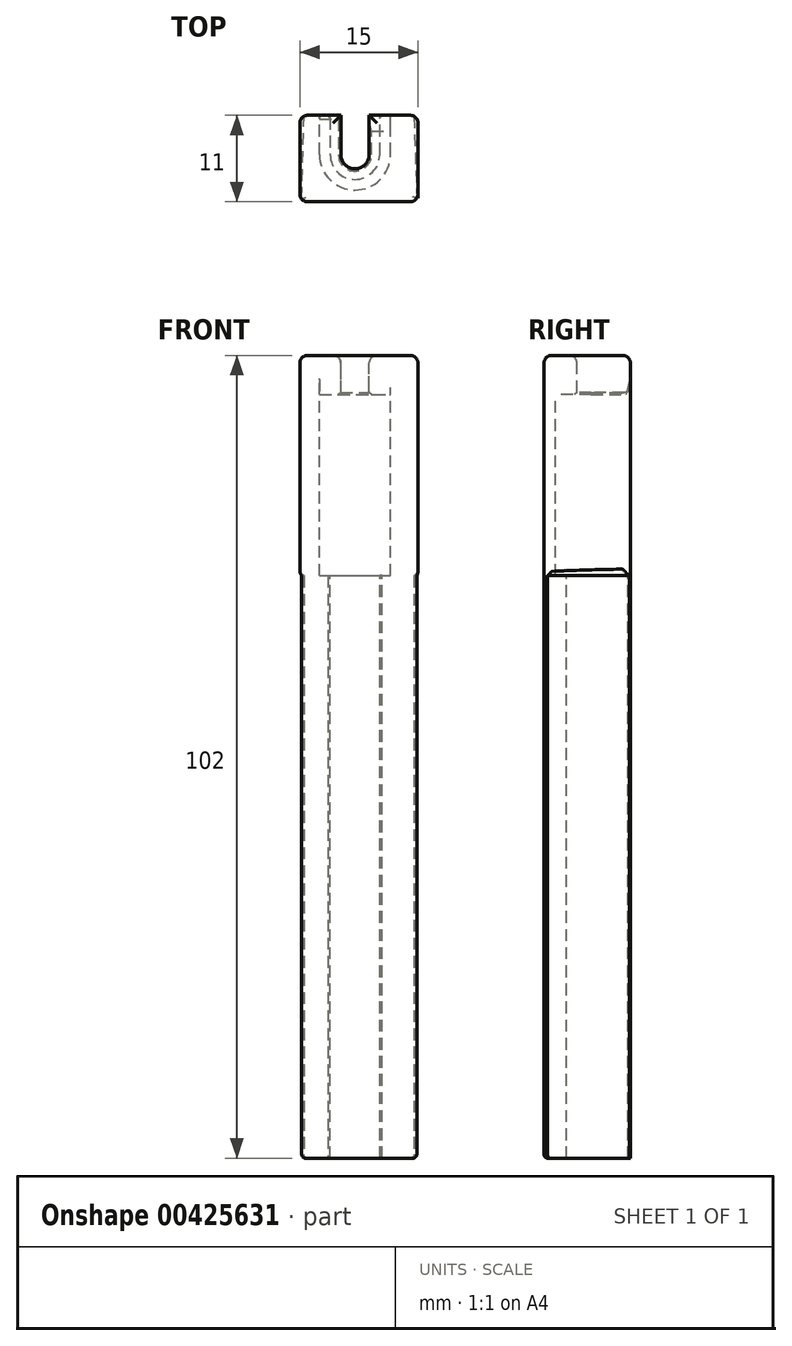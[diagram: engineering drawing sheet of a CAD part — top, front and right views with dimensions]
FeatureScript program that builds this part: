
annotation { "Feature Type Name" : "Feature", "Feature Type Description" : "" }
export const myFeature = defineFeature(function(context is Context, id is Id, definition is map)
    precondition{}
    {
        {
            var Q0;
            Q0=qCreatedBy(makeId("Top.planeOp"),FACE);
            var sketch = newSketch(context, id + "F0", { "sketchPlane" : qUnion([Q0])});
            skLineSegment(sketch, "E0", {"start": v(0, 0) * mm, "end": v(0, 20) * mm});
            skLineSegment(sketch, "E1", {"start": v(0, 20) * mm, "end": v(15, 20) * mm});
            skLineSegment(sketch, "E2", {"start": v(15, 20) * mm, "end": v(15, 0) * mm});
            skLineSegment(sketch, "E3", {"start": v(15, 0) * mm, "end": v(0, 0) * mm});
            skLineSegment(sketch, "E4", {"start": v(0, 11) * mm, "end": v(15, 11) * mm});
            skLineSegment(sketch, "E5", {"start": v(15, 16) * mm, "end": v(0, 16) * mm});
            skSolve(sketch);
        }
        {
            var Q0;
            {var subQ0=sQuery(id+"F0.wireOp",EDGE,"E3");Q0=makeQuery(id+"F0.imprint","IMPRINT",FACE,{"disambiguationData":[TD([[makeQuery(id+"F0.imprint","IMPRINT",EDGE,{"derivedFrom":subQ0}),-1.0]])]});}
            extrude(context, id + "F1", {"entities" : qUnion([Q0]), "depth" : 74 * mm});
        }
        {
            var Q0;
            Q0=makeQuery(id+"F1.opExtrude","CAP_FACE",FACE,{"disambiguationData":[OSD([sQuery(id+"F0.wireOp",EDGE,"E0"),sQuery(id+"F0.wireOp",EDGE,"E1"),sQuery(id+"F0.wireOp",EDGE,"E2"),sQuery(id+"F0.wireOp",EDGE,"E3")])],"isStart":false});
            var sketch = newSketch(context, id + "F2", { "sketchPlane" : qUnion([Q0])});
            skLineSegment(sketch, "E6", {"start": v(7, 11) * mm, "end": v(7, 0) * mm, "construction": true});
            skCircle(sketch, "E7", {"center": v(7, 6) * mm, "radius": 3.15 * mm});
            skLineSegment(sketch, "E8", {"start": v(3.85, 6) * mm, "end": v(3.85, 11) * mm});
            skLineSegment(sketch, "E9", {"start": v(10.15, 6) * mm, "end": v(10.15, 11) * mm});
            skLineSegment(sketch, "E10", {"start": v(10.15, 6) * mm, "end": v(3.85, 6) * mm, "construction": true});
            skSolve(sketch);
        }
        {
            var Q0;
            {var subQ0=sQuery(id+"F2.wireOp",EDGE,"E7");var subQ1=makeQuery(id+"F2.imprint","INTERSECT",VERTEX,{"derivedFrom":[subQ0,sQuery(id+"F2.wireOp",EDGE,"E8")]});Q0=makeQuery(id+"F2.imprint","IMPRINT",FACE,{"disambiguationData":[TD([[makeQuery(id+"F2.imprint","IMPRINT",EDGE,{"disambiguationData":[TD([[subQ1,1.0]])],"derivedFrom":subQ0}),1.0]])]});}
            var Q1;
            {var subQ0=sQuery(id+"F2.wireOp",EDGE,"E8");Q1=makeQuery(id+"F2.imprint","IMPRINT",FACE,{"disambiguationData":[TD([[makeQuery(id+"F2.imprint","IMPRINT",EDGE,{"derivedFrom":subQ0}),-1.0]])]});}
            var Q2;
            {var subQ0=sQuery(id+"F2.wireOp",EDGE,"mLhPDnLy-3AhW-8mAD-WIRb-GXeNga6SbxnZ");var subQ1=sQuery(id+"F2.wireOp",EDGE,"E8");var subQ2=makeQuery(id+"F2.imprint","INTERSECT",VERTEX,{"disambiguationData":[OD(0.0)],"derivedFrom":[subQ1,subQ0]});Q2=makeQuery(id+"F2.imprint","IMPRINT",FACE,{"disambiguationData":[TD([[makeQuery(id+"F2.imprint","IMPRINT",EDGE,{"disambiguationData":[TD([[subQ2,-1.0]])],"derivedFrom":subQ1}),-1.0]])]});}
            var Q3;
            {var subQ0=sQuery(id+"F2.wireOp",EDGE,"llRZHJFs-Bipk-uS7y-r4k3-r3Pt3Prqutk8");var subQ1=sQuery(id+"F2.wireOp",EDGE,"E9");var subQ2=makeQuery(id+"F2.imprint","INTERSECT",VERTEX,{"disambiguationData":[OD(0.0)],"derivedFrom":[subQ1,subQ0]});Q3=makeQuery(id+"F2.imprint","IMPRINT",FACE,{"disambiguationData":[TD([[makeQuery(id+"F2.imprint","IMPRINT",EDGE,{"disambiguationData":[TD([[subQ2,-1.0]])],"derivedFrom":subQ1}),1.0]])]});}
            extrude(context, id + "F3", {"entities" : qUnion([Q0, Q1, Q2, Q3]), "operationType" : NewBodyOperationType.REMOVE, "endBound" : BoundingType.UP_TO_NEXT, "oppositeDirection" : true, "depth" : 25 * mm});
        }
        {
            var Q0;
            Q0=makeQuery(id+"F1.opExtrude","SWEPT_EDGE",EDGE,{"disambiguationData":[OSD([sQuery(id+"F0.wireOp",EDGE,"E0"),sQuery(id+"F0.wireOp",EDGE,"E4")])]});
            chamfer(context, id + "F4", {"entities" : qUnion([Q0]), "chamferType" : ChamferType.TWO_OFFSETS, "width1" : 20 * mm, "oppositeDirection" : false, "width2" : .5 * mm, "tangentPropagation" : true});
        }
        {
            var Q0;
            Q0=makeQuery(id+"F1.opExtrude","SWEPT_EDGE",EDGE,{"disambiguationData":[OSD([sQuery(id+"F0.wireOp",EDGE,"E2"),sQuery(id+"F0.wireOp",EDGE,"E4")])]});
            chamfer(context, id + "F5", {"entities" : qUnion([Q0]), "chamferType" : ChamferType.TWO_OFFSETS, "width1" : .5 * mm, "oppositeDirection" : false, "width2" : 15 * mm, "tangentPropagation" : true});
        }
        {
            var Q0;
            {var subQ10=makeQuery(id+"F1.opExtrude","CAP_EDGE",EDGE,{"disambiguationData":[OSD([sQuery(id+"F0.wireOp",EDGE,"E0")])],"isStart":false});Q0=makeQuery(id+"F2.imprint","IMPRINT",FACE,{"disambiguationData":[TD([[makeQuery(id+"F2.imprint","IMPRINT",EDGE,{"derivedFrom":subQ10}),-1.0]])]});}
            extrude(context, id + "F6", {"entities" : qUnion([Q0]), "operationType" : NewBodyOperationType.ADD, "depth" : 23 * mm});
        }
        {
            var Q0;
            Q0=makeQuery(id+"F6.opExtrude","CAP_FACE",FACE,{"disambiguationData":[OSD([sQuery(id+"F0.wireOp",EDGE,"E0"),sQuery(id+"F0.wireOp",EDGE,"E1"),sQuery(id+"F0.wireOp",EDGE,"E2"),sQuery(id+"F0.wireOp",EDGE,"E3"),sQuery(id+"F2.wireOp",EDGE,"E7"),sQuery(id+"F2.wireOp",EDGE,"E8"),sQuery(id+"F2.wireOp",EDGE,"E9"),sQuery(id+"F2.wireOp",EDGE,"mLhPDnLy-3AhW-8mAD-WIRb-GXeNga6SbxnZ"),sQuery(id+"F2.wireOp",EDGE,"llRZHJFs-Bipk-uS7y-r4k3-r3Pt3Prqutk8")])],"isStart":false});
            var sketch = newSketch(context, id + "F7", { "sketchPlane" : qUnion([Q0])});
            skCircle(sketch, "E11", {"center": v(7, 6) * mm, "radius": 4.5 * mm});
            skLineSegment(sketch, "E12", {"start": v(2.5, 6) * mm, "end": v(2.5, 11) * mm});
            skLineSegment(sketch, "E13", {"start": v(11.5, 6) * mm, "end": v(11.5, 11) * mm});
            skSolve(sketch);
        }
        {
            var Q0;
            {var subQ0=sQuery(id+"F2.wireOp",EDGE,"E7");Q0=makeQuery(id+"F7.imprint","IMPRINT",FACE,{"disambiguationData":[TD([[makeQuery(id+"F7.imprint","IMPRINT",EDGE,{"derivedFrom":makeQuery(id+"F6.opExtrude","CAP_EDGE",EDGE,{"disambiguationData":[OSD([subQ0])],"isStart":false})}),-1.0]])]});}
            var Q1;
            {var subQ0=sQuery(id+"F7.wireOp",EDGE,"E13");Q1=makeQuery(id+"F7.imprint","IMPRINT",FACE,{"disambiguationData":[TD([[makeQuery(id+"F7.imprint","IMPRINT",EDGE,{"derivedFrom":subQ0}),1.0]])]});}
            var Q2;
            {var subQ0=sQuery(id+"F7.wireOp",EDGE,"E12");Q2=makeQuery(id+"F7.imprint","IMPRINT",FACE,{"disambiguationData":[TD([[makeQuery(id+"F7.imprint","IMPRINT",EDGE,{"derivedFrom":subQ0}),-1.0]])]});}
            extrude(context, id + "F8", {"entities" : qUnion([Q0, Q1, Q2]), "operationType" : NewBodyOperationType.REMOVE, "oppositeDirection" : true, "depth" : 23 * mm});
        }
        {
            var Q0;
            Q0=makeQuery(id+"F6.opExtrude","CAP_FACE",FACE,{"disambiguationData":[OSD([sQuery(id+"F0.wireOp",EDGE,"E0"),sQuery(id+"F0.wireOp",EDGE,"E1"),sQuery(id+"F0.wireOp",EDGE,"E2"),sQuery(id+"F0.wireOp",EDGE,"E3"),sQuery(id+"F2.wireOp",EDGE,"E7"),sQuery(id+"F2.wireOp",EDGE,"E8"),sQuery(id+"F2.wireOp",EDGE,"E9"),sQuery(id+"F2.wireOp",EDGE,"mLhPDnLy-3AhW-8mAD-WIRb-GXeNga6SbxnZ"),sQuery(id+"F2.wireOp",EDGE,"llRZHJFs-Bipk-uS7y-r4k3-r3Pt3Prqutk8")])],"isStart":false});
            var Q1;
            {var subQ0=sQuery(id+"F2.wireOp",EDGE,"E7");Q1=makeQuery(id+"F7.imprint","IMPRINT",FACE,{"disambiguationData":[TD([[makeQuery(id+"F7.imprint","IMPRINT",EDGE,{"derivedFrom":makeQuery(id+"F6.opExtrude","CAP_EDGE",EDGE,{"disambiguationData":[OSD([subQ0])],"isStart":false})}),-1.0]])]});}
            var Q2;
            {var subQ0=sQuery(id+"F7.wireOp",EDGE,"E12");Q2=makeQuery(id+"F7.imprint","IMPRINT",FACE,{"disambiguationData":[TD([[makeQuery(id+"F7.imprint","IMPRINT",EDGE,{"derivedFrom":subQ0}),-1.0]])]});}
            var Q3;
            {var subQ0=sQuery(id+"F7.wireOp",EDGE,"E13");Q3=makeQuery(id+"F7.imprint","IMPRINT",FACE,{"disambiguationData":[TD([[makeQuery(id+"F7.imprint","IMPRINT",EDGE,{"derivedFrom":subQ0}),1.0]])]});}
            extrude(context, id + "F9", {"entities" : qUnion([Q0, Q1, Q2, Q3]), "operationType" : NewBodyOperationType.ADD, "depth" : 5 * mm});
        }
        {
            var Q0;
            {var subQ0=sQuery(id+"F2.wireOp",EDGE,"llRZHJFs-Bipk-uS7y-r4k3-r3Pt3Prqutk8");var subQ1=sQuery(id+"F2.wireOp",EDGE,"mLhPDnLy-3AhW-8mAD-WIRb-GXeNga6SbxnZ");var subQ2=sQuery(id+"F2.wireOp",EDGE,"E9");var subQ3=sQuery(id+"F2.wireOp",EDGE,"E8");var subQ4=sQuery(id+"F2.wireOp",EDGE,"E7");var subQ5=sQuery(id+"F0.wireOp",EDGE,"E1");Q0=makeQuery(id+"F9.boolean.opBoolean","MERGE",FACE,{"derivedFrom":[makeQuery(id+"F9.opExtrude","CAP_FACE",FACE,{"disambiguationData":[OSD([subQ5,subQ4,subQ3,subQ2,subQ1,subQ0,sQuery(id+"F7.wireOp",EDGE,"E11"),sQuery(id+"F7.wireOp",EDGE,"E12"),sQuery(id+"F7.wireOp",EDGE,"E13")])],"isStart":false}),makeQuery(id+"F9.opExtrude","CAP_FACE",FACE,{"disambiguationData":[OSD([sQuery(id+"F0.wireOp",EDGE,"E0"),subQ5,sQuery(id+"F0.wireOp",EDGE,"E2"),sQuery(id+"F0.wireOp",EDGE,"E3"),subQ4,subQ3,subQ2,subQ1,subQ0])],"isStart":false})]});}
            var sketch = newSketch(context, id + "F10", { "sketchPlane" : qUnion([Q0])});
            skCircle(sketch, "E14", {"center": v(7, 6) * mm, "radius": 1.8 * mm});
            skLineSegment(sketch, "E15", {"start": v(7, 6) * mm, "end": v(0, 6) * mm});
            skLineSegment(sketch, "E16", {"start": v(7, 6) * mm, "end": v(15, 6) * mm});
            skLineSegment(sketch, "E17", {"start": v(3.85, 11) * mm, "end": v(10.15, 11) * mm});
            skLineSegment(sketch, "E18", {"start": v(5.2, 6) * mm, "end": v(5.2, 11) * mm});
            skLineSegment(sketch, "E19", {"start": v(8.8, 6) * mm, "end": v(8.8, 11) * mm});
            skSolve(sketch);
        }
        {
            var Q0;
            {var subQ6=sQuery(id+"F2.wireOp",EDGE,"E7");var subQ7=makeQuery(id+"F9.opExtrude","CAP_EDGE",EDGE,{"disambiguationData":[OSD([subQ6])],"isStart":false});Q0=makeQuery(id+"F10.imprint","IMPRINT",FACE,{"disambiguationData":[TD([[makeQuery(id+"F10.imprint","IMPRINT",EDGE,{"derivedFrom":subQ7}),1.0]])]});}
            var Q1;
            {var subQ3=sQuery(id+"F10.wireOp",EDGE,"E18");Q1=makeQuery(id+"F10.imprint","IMPRINT",FACE,{"disambiguationData":[TD([[makeQuery(id+"F10.imprint","IMPRINT",EDGE,{"derivedFrom":subQ3}),1.0]])]});}
            var Q2;
            {var subQ3=sQuery(id+"F10.wireOp",EDGE,"E19");Q2=makeQuery(id+"F10.imprint","IMPRINT",FACE,{"disambiguationData":[TD([[makeQuery(id+"F10.imprint","IMPRINT",EDGE,{"derivedFrom":subQ3}),-1.0]])]});}
            extrude(context, id + "F11", {"entities" : qUnion([Q0, Q1, Q2]), "operationType" : NewBodyOperationType.ADD, "oppositeDirection" : true, "depth" : 5 * mm});
        }
        {
            var Q0;
            Q0=makeQuery(id+"F11.opExtrude","CAP_EDGE",EDGE,{"disambiguationData":[OSD([sQuery(id+"F10.wireOp",EDGE,"E14")])],"isStart":false});
            var Q1;
            Q1=makeQuery(id+"F11.opExtrude","CAP_EDGE",EDGE,{"disambiguationData":[OSD([sQuery(id+"F10.wireOp",EDGE,"E15")])],"isStart":false});
            var Q2;
            Q2=makeQuery(id+"F11.opExtrude","CAP_EDGE",EDGE,{"disambiguationData":[OSD([sQuery(id+"F10.wireOp",EDGE,"E16")])],"isStart":false});
            var Q3;
            Q3=makeQuery(id+"F11.opExtrude","SWEPT_EDGE",EDGE,{"disambiguationData":[OSD([sQuery(id+"F10.wireOp",EDGE,"E14"),sQuery(id+"F10.wireOp",EDGE,"E16")])]});
            var Q4;
            Q4=makeQuery(id+"F11.opExtrude","SWEPT_EDGE",EDGE,{"disambiguationData":[OSD([sQuery(id+"F10.wireOp",EDGE,"E14"),sQuery(id+"F10.wireOp",EDGE,"E15")])]});
            var Q5;
            Q5=makeQuery(id+"F9.opExtrude","SWEPT_EDGE",EDGE,{"disambiguationData":[OSD([sQuery(id+"F0.wireOp",EDGE,"E1"),sQuery(id+"F2.wireOp",EDGE,"E8")])]});
            var Q6;
            Q6=makeQuery(id+"F9.opExtrude","SWEPT_EDGE",EDGE,{"disambiguationData":[OSD([sQuery(id+"F0.wireOp",EDGE,"E1"),sQuery(id+"F2.wireOp",EDGE,"E9")])]});
            var Q7;
            {var subQ0=sQuery(id+"F2.wireOp",EDGE,"E9");var subQ1=sQuery(id+"F0.wireOp",EDGE,"E4");var subQ2=sQuery(id+"F2.wireOp",EDGE,"E7");Q7=qUnion([makeQuery(id+"F6.boolean.opBoolean","MERGE",EDGE,{"derivedFrom":[makeQuery(id+"F3.boolean.opBoolean","COPY",EDGE,{"derivedFrom":makeQuery(id+"F3.opExtrude","SWEPT_EDGE",EDGE,{"disambiguationData":[OSD([subQ2,subQ0])]})}),makeQuery(id+"F6.opExtrude","SWEPT_EDGE",EDGE,{"disambiguationData":[OSD([subQ2,subQ0])]})]}),makeQuery(id+"F6.boolean.opBoolean","MERGE",EDGE,{"derivedFrom":[makeQuery(id+"F3.boolean.opBoolean","COPY",EDGE,{"derivedFrom":makeQuery(id+"F3.opExtrude","SWEPT_EDGE",EDGE,{"disambiguationData":[OSD([subQ1,subQ0])]})}),makeQuery(id+"F6.opExtrude","SWEPT_EDGE",EDGE,{"disambiguationData":[OSD([subQ1,subQ0])]})]})]);}
            var Q8;
            {var subQ0=sQuery(id+"F2.wireOp",EDGE,"E8");var subQ1=sQuery(id+"F0.wireOp",EDGE,"E4");var subQ2=sQuery(id+"F2.wireOp",EDGE,"E7");Q8=qUnion([makeQuery(id+"F6.boolean.opBoolean","MERGE",EDGE,{"derivedFrom":[makeQuery(id+"F3.boolean.opBoolean","COPY",EDGE,{"derivedFrom":makeQuery(id+"F3.opExtrude","SWEPT_EDGE",EDGE,{"disambiguationData":[OSD([subQ2,subQ0])]})}),makeQuery(id+"F6.opExtrude","SWEPT_EDGE",EDGE,{"disambiguationData":[OSD([subQ2,subQ0])]})]}),makeQuery(id+"F6.boolean.opBoolean","MERGE",EDGE,{"derivedFrom":[makeQuery(id+"F3.boolean.opBoolean","COPY",EDGE,{"derivedFrom":makeQuery(id+"F3.opExtrude","SWEPT_EDGE",EDGE,{"disambiguationData":[OSD([subQ1,subQ0])]})}),makeQuery(id+"F6.opExtrude","SWEPT_EDGE",EDGE,{"disambiguationData":[OSD([subQ1,subQ0])]})]})]);}
            chamfer(context, id + "F12", {"entities" : qUnion([Q0, Q1, Q2, Q3, Q4, Q5, Q6, Q7, Q8]), "width" : .3 * mm, "tangentPropagation" : true});
        }
        {
            var Q0;
            {var subQ0=sQuery(id+"F2.wireOp",EDGE,"E7");var subQ1=sQuery(id+"F2.wireOp",EDGE,"llRZHJFs-Bipk-uS7y-r4k3-r3Pt3Prqutk8");var subQ2=sQuery(id+"F2.wireOp",EDGE,"mLhPDnLy-3AhW-8mAD-WIRb-GXeNga6SbxnZ");var subQ3=sQuery(id+"F2.wireOp",EDGE,"E9");var subQ4=sQuery(id+"F2.wireOp",EDGE,"E8");var subQ5=sQuery(id+"F0.wireOp",EDGE,"E1");Q0=makeQuery(id+"F11.boolean.opBoolean","MERGE",FACE,{"derivedFrom":[makeQuery(id+"F9.boolean.opBoolean","MERGE",FACE,{"derivedFrom":[makeQuery(id+"F9.opExtrude","CAP_FACE",FACE,{"disambiguationData":[OSD([subQ5,subQ0,subQ4,subQ3,subQ2,subQ1,sQuery(id+"F7.wireOp",EDGE,"E11"),sQuery(id+"F7.wireOp",EDGE,"E12"),sQuery(id+"F7.wireOp",EDGE,"E13")])],"isStart":false}),makeQuery(id+"F9.opExtrude","CAP_FACE",FACE,{"disambiguationData":[OSD([sQuery(id+"F0.wireOp",EDGE,"E0"),subQ5,sQuery(id+"F0.wireOp",EDGE,"E2"),sQuery(id+"F0.wireOp",EDGE,"E3"),subQ0,subQ4,subQ3,subQ2,subQ1])],"isStart":false})]}),makeQuery(id+"F11.opExtrude","CAP_FACE",FACE,{"disambiguationData":[OSD([subQ0,sQuery(id+"F10.wireOp",EDGE,"E14"),sQuery(id+"F10.wireOp",EDGE,"E15"),sQuery(id+"F10.wireOp",EDGE,"E16")])],"isStart":true})]});}
            var Q1;
            {var subQ0=sQuery(id+"F0.wireOp",EDGE,"E2");Q1=makeQuery(id+"F9.boolean.opBoolean","MERGE",FACE,{"derivedFrom":[makeQuery(id+"F6.boolean.opBoolean","MERGE",FACE,{"derivedFrom":[makeQuery(id+"F1.opExtrude","SWEPT_FACE",FACE,{"disambiguationData":[OSD([subQ0])]}),makeQuery(id+"F6.opExtrude","SWEPT_FACE",FACE,{"disambiguationData":[OSD([subQ0])]})]}),makeQuery(id+"F9.opExtrude","SWEPT_FACE",FACE,{"disambiguationData":[OSD([subQ0])]})]});}
            var Q2;
            Q2=makeQuery(id+"F6.opExtrude","CAP_EDGE",EDGE,{"disambiguationData":[OSD([sQuery(id+"F0.wireOp",EDGE,"E2")])],"isStart":true});
            var Q3;
            {var subQ0=sQuery(id+"F0.wireOp",EDGE,"E0");Q3=makeQuery(id+"F9.boolean.opBoolean","MERGE",FACE,{"derivedFrom":[makeQuery(id+"F6.opExtrude","SWEPT_FACE",FACE,{"disambiguationData":[OSD([subQ0])]}),makeQuery(id+"F9.opExtrude","SWEPT_FACE",FACE,{"disambiguationData":[OSD([subQ0])]})]});}
            fillet(context, id + "F13", {"entities" : qUnion([Q0, Q1, Q2, Q3]), "radius" : 1 * mm, "tangentPropagation" : true, "allowEdgeOverflow" : false});
        }
        {
            var Q0;
            Q0=makeQuery(id+"F9.opExtrude","CAP_EDGE",EDGE,{"disambiguationData":[OSD([sQuery(id+"F0.wireOp",EDGE,"E3")])],"isStart":false});
            var Q1;
            {var subQ0=sQuery(id+"F0.wireOp",EDGE,"E3");var subQ1=sQuery(id+"F0.wireOp",EDGE,"E0");Q1=makeQuery(id+"F9.boolean.opBoolean","MERGE",EDGE,{"derivedFrom":[makeQuery(id+"F6.opExtrude","SWEPT_EDGE",EDGE,{"disambiguationData":[OSD([subQ1,subQ0])]}),makeQuery(id+"F9.opExtrude","SWEPT_EDGE",EDGE,{"disambiguationData":[OSD([subQ1,subQ0])]})]});}
            var Q2;
            {var subQ0=sQuery(id+"F0.wireOp",EDGE,"E3");var subQ1=sQuery(id+"F0.wireOp",EDGE,"E2");Q2=makeQuery(id+"F9.boolean.opBoolean","MERGE",EDGE,{"derivedFrom":[makeQuery(id+"F6.boolean.opBoolean","MERGE",EDGE,{"derivedFrom":[makeQuery(id+"F1.opExtrude","SWEPT_EDGE",EDGE,{"disambiguationData":[OSD([subQ1,subQ0])]}),makeQuery(id+"F6.opExtrude","SWEPT_EDGE",EDGE,{"disambiguationData":[OSD([subQ1,subQ0])]})]}),makeQuery(id+"F9.opExtrude","SWEPT_EDGE",EDGE,{"disambiguationData":[OSD([subQ1,subQ0])]})]});}
            var Q3;
            {var subQ1=sQuery(id+"F0.wireOp",EDGE,"E2");var subQ2=sQuery(id+"F0.wireOp",EDGE,"E1");Q3=makeQuery(id+"F5.opChamfer","BLEND_EDGE",EDGE,{"blendedFrom":[makeQuery(id+"F1.opExtrude","SWEPT_EDGE",EDGE,{"disambiguationData":[OSD([subQ2,subQ1])]}),makeQuery(id+"F3.boolean.opBoolean","SPLIT",FACE,{"disambiguationData":[TD([makeQuery(id+"F1.opExtrude","SWEPT_FACE",FACE,{"disambiguationData":[OSD([subQ1])]})])],"derivedFrom":makeQuery(id+"F1.opExtrude","SWEPT_FACE",FACE,{"disambiguationData":[OSD([subQ2])]})})],"blendedInto":[makeQuery(id+"F3.boolean.opBoolean","SPLIT",FACE,{"disambiguationData":[TD([makeQuery(id+"F1.opExtrude","SWEPT_FACE",FACE,{"disambiguationData":[OSD([subQ1])]})])],"derivedFrom":makeQuery(id+"F1.opExtrude","SWEPT_FACE",FACE,{"disambiguationData":[OSD([subQ2])]})})]});}
            var Q4;
            {var subQ0=sQuery(id+"F0.wireOp",EDGE,"E0");var subQ3=sQuery(id+"F0.wireOp",EDGE,"E1");Q4=makeQuery(id+"F4.opChamfer","BLEND_EDGE",EDGE,{"blendedFrom":[makeQuery(id+"F1.opExtrude","SWEPT_EDGE",EDGE,{"disambiguationData":[OSD([subQ0,subQ3])]}),makeQuery(id+"F3.boolean.opBoolean","SPLIT",FACE,{"disambiguationData":[TD([makeQuery(id+"F1.opExtrude","SWEPT_FACE",FACE,{"disambiguationData":[OSD([subQ0])]})])],"derivedFrom":makeQuery(id+"F1.opExtrude","SWEPT_FACE",FACE,{"disambiguationData":[OSD([subQ3])]})})],"blendedInto":[makeQuery(id+"F3.boolean.opBoolean","SPLIT",FACE,{"disambiguationData":[TD([makeQuery(id+"F1.opExtrude","SWEPT_FACE",FACE,{"disambiguationData":[OSD([subQ0])]})])],"derivedFrom":makeQuery(id+"F1.opExtrude","SWEPT_FACE",FACE,{"disambiguationData":[OSD([subQ3])]})})]});}
            var Q5;
            {var subQ0=sQuery(id+"F0.wireOp",EDGE,"E1");var subQ1=sQuery(id+"F0.wireOp",EDGE,"E0");Q5=makeQuery(id+"F9.boolean.opBoolean","MERGE",EDGE,{"derivedFrom":[makeQuery(id+"F6.opExtrude","SWEPT_EDGE",EDGE,{"disambiguationData":[OSD([subQ1,subQ0])]}),makeQuery(id+"F9.opExtrude","SWEPT_EDGE",EDGE,{"disambiguationData":[OSD([subQ1,subQ0])]})]});}
            var Q6;
            {var subQ0=sQuery(id+"F0.wireOp",EDGE,"E2");var subQ1=sQuery(id+"F0.wireOp",EDGE,"E1");Q6=makeQuery(id+"F9.boolean.opBoolean","MERGE",EDGE,{"derivedFrom":[makeQuery(id+"F6.opExtrude","SWEPT_EDGE",EDGE,{"disambiguationData":[OSD([subQ1,subQ0])]}),makeQuery(id+"F9.opExtrude","SWEPT_EDGE",EDGE,{"disambiguationData":[OSD([subQ1,subQ0])]})]});}
            var Q7;
            Q7=makeQuery(id+"F1.opExtrude","CAP_EDGE",EDGE,{"disambiguationData":[OSD([sQuery(id+"F0.wireOp",EDGE,"E3")])],"isStart":true});
            var Q8;
            Q8=makeQuery(id+"F3.boolean.opBoolean","COPY",EDGE,{"derivedFrom":makeQuery(id+"F3.opExtrude","CAP_EDGE",EDGE,{"disambiguationData":[OSD([sQuery(id+"F2.wireOp",EDGE,"E9")])],"isStart":false})});
            var Q9;
            {var subQ0=sQuery(id+"F0.wireOp",EDGE,"E4");var subQ1=sQuery(id+"F0.wireOp",EDGE,"E2");Q9=makeQuery(id+"F5.opChamfer","BLEND_EDGE",EDGE,{"blendedFrom":[makeQuery(id+"F1.opExtrude","SWEPT_EDGE",EDGE,{"disambiguationData":[OSD([subQ1,subQ0])]}),makeQuery(id+"F1.opExtrude","CAP_FACE",FACE,{"disambiguationData":[OSD([sQuery(id+"F0.wireOp",EDGE,"E0"),subQ1,sQuery(id+"F0.wireOp",EDGE,"E3"),subQ0])],"isStart":true})],"blendedInto":[makeQuery(id+"F1.opExtrude","CAP_FACE",FACE,{"disambiguationData":[OSD([sQuery(id+"F0.wireOp",EDGE,"E0"),subQ1,sQuery(id+"F0.wireOp",EDGE,"E3"),subQ0])],"isStart":true})]});}
            var Q10;
            {var subQ0=sQuery(id+"F0.wireOp",EDGE,"E4");var subQ1=sQuery(id+"F0.wireOp",EDGE,"E0");Q10=makeQuery(id+"F4.opChamfer","BLEND_EDGE",EDGE,{"blendedFrom":[makeQuery(id+"F1.opExtrude","SWEPT_EDGE",EDGE,{"disambiguationData":[OSD([subQ1,subQ0])]}),makeQuery(id+"F1.opExtrude","CAP_FACE",FACE,{"disambiguationData":[OSD([subQ1,sQuery(id+"F0.wireOp",EDGE,"E2"),sQuery(id+"F0.wireOp",EDGE,"E3"),subQ0])],"isStart":true})],"blendedInto":[makeQuery(id+"F1.opExtrude","CAP_FACE",FACE,{"disambiguationData":[OSD([subQ1,sQuery(id+"F0.wireOp",EDGE,"E2"),sQuery(id+"F0.wireOp",EDGE,"E3"),subQ0])],"isStart":true})]});}
            var Q11;
            {var subQ0=sQuery(id+"F0.wireOp",EDGE,"E0");var subQ1=sQuery(id+"F0.wireOp",EDGE,"E4");Q11=makeQuery(id+"F4.opChamfer","BLEND_EDGE",EDGE,{"blendedFrom":[makeQuery(id+"F1.opExtrude","SWEPT_EDGE",EDGE,{"disambiguationData":[OSD([subQ0,subQ1])]}),makeQuery(id+"F3.boolean.opBoolean","SPLIT",FACE,{"disambiguationData":[TD([makeQuery(id+"F1.opExtrude","SWEPT_FACE",FACE,{"disambiguationData":[OSD([subQ0])]})])],"derivedFrom":makeQuery(id+"F1.opExtrude","SWEPT_FACE",FACE,{"disambiguationData":[OSD([subQ1])]})})],"blendedInto":[makeQuery(id+"F3.boolean.opBoolean","SPLIT",FACE,{"disambiguationData":[TD([makeQuery(id+"F1.opExtrude","SWEPT_FACE",FACE,{"disambiguationData":[OSD([subQ0])]})])],"derivedFrom":makeQuery(id+"F1.opExtrude","SWEPT_FACE",FACE,{"disambiguationData":[OSD([subQ1])]})})]});}
            fillet(context, id + "F14", {"entities" : qUnion([Q0, Q1, Q2, Q3, Q4, Q5, Q6, Q7, Q8, Q9, Q10, Q11]), "radius" : .5 * mm, "tangentPropagation" : true, "allowEdgeOverflow" : false});
        }
        {
            var Q0;
            {var subQ0=sQuery(id+"F0.wireOp",EDGE,"E4");var subQ1=makeQuery(id+"F1.opExtrude","CAP_EDGE",EDGE,{"disambiguationData":[OSD([subQ0])],"isStart":false});var subQ2=sQuery(id+"F2.wireOp",EDGE,"E8");var subQ3=makeQuery(id+"F6.opExtrude","CAP_EDGE",EDGE,{"disambiguationData":[OSD([subQ0]),TDD([makeQuery(id+"F2.imprint","IMPRINT",EDGE,{"disambiguationData":[TD([[makeQuery(id+"F2.imprint","INTERSECT",VERTEX,{"derivedFrom":[makeQuery(id+"F1.opExtrude","CAP_EDGE",EDGE,{"disambiguationData":[OSD([sQuery(id+"F0.wireOp",EDGE,"E0")])],"isStart":false}),subQ1]}),-1.0]])],"derivedFrom":subQ1})])],"isStart":false});Q0=makeQuery(id+"F8.boolean.opBoolean","COPY",EDGE,{"derivedFrom":makeQuery(id+"F8.opExtrude","CAP_EDGE",EDGE,{"disambiguationData":[OSD([subQ0]),TDD([makeQuery(id+"F7.imprint","IMPRINT",EDGE,{"disambiguationData":[TD([[makeQuery(id+"F7.imprint","INTERSECT",VERTEX,{"derivedFrom":[makeQuery(id+"F6.opExtrude","CAP_EDGE",EDGE,{"disambiguationData":[OSD([subQ2])],"isStart":false}),subQ3]}),1.0]])],"derivedFrom":subQ3})])],"isStart":false})});}
            var Q1;
            {var subQ0=sQuery(id+"F0.wireOp",EDGE,"E4");var subQ1=makeQuery(id+"F1.opExtrude","CAP_EDGE",EDGE,{"disambiguationData":[OSD([subQ0])],"isStart":false});var subQ2=sQuery(id+"F2.wireOp",EDGE,"E9");var subQ3=makeQuery(id+"F6.opExtrude","CAP_EDGE",EDGE,{"disambiguationData":[OSD([subQ0]),TDD([makeQuery(id+"F2.imprint","IMPRINT",EDGE,{"disambiguationData":[TD([[makeQuery(id+"F2.imprint","INTERSECT",VERTEX,{"derivedFrom":[makeQuery(id+"F1.opExtrude","CAP_EDGE",EDGE,{"disambiguationData":[OSD([sQuery(id+"F0.wireOp",EDGE,"E2")])],"isStart":false}),subQ1]}),1.0]])],"derivedFrom":subQ1})])],"isStart":false});Q1=makeQuery(id+"F8.boolean.opBoolean","COPY",EDGE,{"derivedFrom":makeQuery(id+"F8.opExtrude","CAP_EDGE",EDGE,{"disambiguationData":[OSD([subQ0]),TDD([makeQuery(id+"F7.imprint","IMPRINT",EDGE,{"disambiguationData":[TD([[makeQuery(id+"F7.imprint","INTERSECT",VERTEX,{"derivedFrom":[makeQuery(id+"F6.opExtrude","CAP_EDGE",EDGE,{"disambiguationData":[OSD([subQ2])],"isStart":false}),subQ3]}),-1.0]])],"derivedFrom":subQ3})])],"isStart":false})});}
            var Q2;
            {var subQ0=sQuery(id+"F10.wireOp",EDGE,"E17");var subQ1=sQuery(id+"F0.wireOp",EDGE,"E4");var subQ2=makeQuery(id+"F1.opExtrude","CAP_EDGE",EDGE,{"disambiguationData":[OSD([subQ1])],"isStart":false});var subQ3=sQuery(id+"F2.wireOp",EDGE,"E8");var subQ4=makeQuery(id+"F6.opExtrude","CAP_EDGE",EDGE,{"disambiguationData":[OSD([subQ1]),TDD([makeQuery(id+"F2.imprint","IMPRINT",EDGE,{"disambiguationData":[TD([[makeQuery(id+"F2.imprint","INTERSECT",VERTEX,{"derivedFrom":[makeQuery(id+"F1.opExtrude","CAP_EDGE",EDGE,{"disambiguationData":[OSD([sQuery(id+"F0.wireOp",EDGE,"E0")])],"isStart":false}),subQ2]}),-1.0]])],"derivedFrom":subQ2})])],"isStart":false});var subQ5=subQ4;var subQ6=makeQuery(id+"F7.imprint","IMPRINT",EDGE,{"disambiguationData":[TD([[makeQuery(id+"F7.imprint","INTERSECT",VERTEX,{"derivedFrom":[makeQuery(id+"F6.opExtrude","CAP_EDGE",EDGE,{"disambiguationData":[OSD([subQ3])],"isStart":false}),subQ4]}),1.0]])],"derivedFrom":subQ4});Q2=makeQuery(id+"F11.boolean.opBoolean","MERGE",EDGE,{"derivedFrom":[makeQuery(id+"F9.boolean.opBoolean","MERGE",EDGE,{"derivedFrom":[makeQuery(id+"F9.opExtrude","CAP_EDGE",EDGE,{"disambiguationData":[OSD([subQ1]),TDD([subQ6])],"isStart":true}),makeQuery(id+"F9.opExtrude","CAP_EDGE",EDGE,{"disambiguationData":[OSD([subQ1]),TDD([subQ5])],"isStart":true})]}),makeQuery(id+"F11.opExtrude","CAP_EDGE",EDGE,{"disambiguationData":[OSD([subQ0]),TDD([makeQuery(id+"F10.imprint","IMPRINT",EDGE,{"disambiguationData":[TD([[makeQuery(id+"F10.imprint","INTERSECT",VERTEX,{"derivedFrom":[subQ0,sQuery(id+"F10.wireOp",EDGE,"E18")]}),1.0]])],"derivedFrom":subQ0})])],"isStart":false})]});}
            chamfer(context, id + "F15", {"entities" : qUnion([Q0, Q1, Q2]), "chamferType" : ChamferType.TWO_OFFSETS, "width1" : .5 * mm, "oppositeDirection" : false, "width2" : 2 * mm});
        }
        {
            var Q0;
            {var subQ0=sQuery(id+"F10.wireOp",EDGE,"E17");var subQ1=sQuery(id+"F0.wireOp",EDGE,"E4");var subQ2=makeQuery(id+"F1.opExtrude","CAP_EDGE",EDGE,{"disambiguationData":[OSD([subQ1])],"isStart":false});var subQ3=sQuery(id+"F2.wireOp",EDGE,"E9");var subQ4=makeQuery(id+"F6.opExtrude","CAP_EDGE",EDGE,{"disambiguationData":[OSD([subQ1]),TDD([makeQuery(id+"F2.imprint","IMPRINT",EDGE,{"disambiguationData":[TD([[makeQuery(id+"F2.imprint","INTERSECT",VERTEX,{"derivedFrom":[makeQuery(id+"F1.opExtrude","CAP_EDGE",EDGE,{"disambiguationData":[OSD([sQuery(id+"F0.wireOp",EDGE,"E2")])],"isStart":false}),subQ2]}),1.0]])],"derivedFrom":subQ2})])],"isStart":false});var subQ5=subQ4;var subQ6=makeQuery(id+"F7.imprint","IMPRINT",EDGE,{"disambiguationData":[TD([[makeQuery(id+"F7.imprint","INTERSECT",VERTEX,{"derivedFrom":[makeQuery(id+"F6.opExtrude","CAP_EDGE",EDGE,{"disambiguationData":[OSD([subQ3])],"isStart":false}),subQ4]}),-1.0]])],"derivedFrom":subQ4});Q0=makeQuery(id+"F11.boolean.opBoolean","MERGE",EDGE,{"derivedFrom":[makeQuery(id+"F9.boolean.opBoolean","MERGE",EDGE,{"derivedFrom":[makeQuery(id+"F9.opExtrude","CAP_EDGE",EDGE,{"disambiguationData":[OSD([subQ1]),TDD([subQ6])],"isStart":true}),makeQuery(id+"F9.opExtrude","CAP_EDGE",EDGE,{"disambiguationData":[OSD([subQ1]),TDD([subQ5])],"isStart":true})]}),makeQuery(id+"F11.opExtrude","CAP_EDGE",EDGE,{"disambiguationData":[OSD([subQ0]),TDD([makeQuery(id+"F10.imprint","IMPRINT",EDGE,{"disambiguationData":[TD([[makeQuery(id+"F10.imprint","INTERSECT",VERTEX,{"derivedFrom":[subQ0,sQuery(id+"F10.wireOp",EDGE,"E19")]}),-1.0]])],"derivedFrom":subQ0})])],"isStart":false})]});}
            chamfer(context, id + "F16", {"entities" : qUnion([Q0]), "chamferType" : ChamferType.TWO_OFFSETS, "width1" : 2 * mm, "oppositeDirection" : false, "width2" : .5 * mm, "tangentPropagation" : true});
        }
        {
            var Q0;
            {var subQ0=sQuery(id+"F10.wireOp",EDGE,"E17");var subQ1=sQuery(id+"F0.wireOp",EDGE,"E4");var subQ2=makeQuery(id+"F1.opExtrude","CAP_EDGE",EDGE,{"disambiguationData":[OSD([subQ1])],"isStart":false});var subQ3=sQuery(id+"F0.wireOp",EDGE,"E2");var subQ4=sQuery(id+"F2.wireOp",EDGE,"E9");var subQ5=makeQuery(id+"F2.imprint","IMPRINT",EDGE,{"disambiguationData":[TD([[makeQuery(id+"F2.imprint","INTERSECT",VERTEX,{"derivedFrom":[makeQuery(id+"F1.opExtrude","CAP_EDGE",EDGE,{"disambiguationData":[OSD([subQ3])],"isStart":false}),subQ2]}),1.0]])],"derivedFrom":subQ2});var subQ6=makeQuery(id+"F6.opExtrude","CAP_EDGE",EDGE,{"disambiguationData":[OSD([subQ1]),TDD([subQ5])],"isStart":false});var subQ7=subQ6;var subQ8=makeQuery(id+"F7.imprint","IMPRINT",EDGE,{"disambiguationData":[TD([[makeQuery(id+"F7.imprint","INTERSECT",VERTEX,{"derivedFrom":[makeQuery(id+"F6.opExtrude","CAP_EDGE",EDGE,{"disambiguationData":[OSD([subQ4])],"isStart":false}),subQ6]}),-1.0]])],"derivedFrom":subQ6});Q0=makeQuery(id+"F15.opChamfer","BLEND_EDGE",EDGE,{"blendedFrom":[makeQuery(id+"F8.boolean.opBoolean","COPY",EDGE,{"derivedFrom":makeQuery(id+"F8.opExtrude","CAP_EDGE",EDGE,{"disambiguationData":[OSD([subQ1]),TDD([subQ8])],"isStart":false})}),makeQuery(id+"F11.boolean.opBoolean","MERGE",FACE,{"derivedFrom":[makeQuery(id+"F9.boolean.opBoolean","MERGE",FACE,{"derivedFrom":[makeQuery(id+"F6.boolean.opBoolean","MERGE",FACE,{"derivedFrom":[makeQuery(id+"F3.boolean.opBoolean","SPLIT",FACE,{"disambiguationData":[TD([makeQuery(id+"F1.opExtrude","SWEPT_FACE",FACE,{"disambiguationData":[OSD([subQ3])]})])],"derivedFrom":makeQuery(id+"F1.opExtrude","SWEPT_FACE",FACE,{"disambiguationData":[OSD([subQ1])]})}),makeQuery(id+"F6.opExtrude","SWEPT_FACE",FACE,{"disambiguationData":[OSD([subQ1]),TDD([subQ5])]})]}),makeQuery(id+"F9.opExtrude","SWEPT_FACE",FACE,{"disambiguationData":[OSD([subQ1]),TDD([subQ8])]}),makeQuery(id+"F9.opExtrude","SWEPT_FACE",FACE,{"disambiguationData":[OSD([subQ1]),TDD([subQ7])]})]}),makeQuery(id+"F11.opExtrude","SWEPT_FACE",FACE,{"disambiguationData":[OSD([subQ0]),TDD([makeQuery(id+"F10.imprint","IMPRINT",EDGE,{"disambiguationData":[TD([[makeQuery(id+"F10.imprint","INTERSECT",VERTEX,{"derivedFrom":[subQ0,sQuery(id+"F10.wireOp",EDGE,"E19")]}),-1.0]])],"derivedFrom":subQ0})])]})]})],"blendedInto":[makeQuery(id+"F11.boolean.opBoolean","MERGE",FACE,{"derivedFrom":[makeQuery(id+"F9.boolean.opBoolean","MERGE",FACE,{"derivedFrom":[makeQuery(id+"F6.boolean.opBoolean","MERGE",FACE,{"derivedFrom":[makeQuery(id+"F3.boolean.opBoolean","SPLIT",FACE,{"disambiguationData":[TD([makeQuery(id+"F1.opExtrude","SWEPT_FACE",FACE,{"disambiguationData":[OSD([subQ3])]})])],"derivedFrom":makeQuery(id+"F1.opExtrude","SWEPT_FACE",FACE,{"disambiguationData":[OSD([subQ1])]})}),makeQuery(id+"F6.opExtrude","SWEPT_FACE",FACE,{"disambiguationData":[OSD([subQ1]),TDD([subQ5])]})]}),makeQuery(id+"F9.opExtrude","SWEPT_FACE",FACE,{"disambiguationData":[OSD([subQ1]),TDD([subQ8])]}),makeQuery(id+"F9.opExtrude","SWEPT_FACE",FACE,{"disambiguationData":[OSD([subQ1]),TDD([subQ7])]})]}),makeQuery(id+"F11.opExtrude","SWEPT_FACE",FACE,{"disambiguationData":[OSD([subQ0]),TDD([makeQuery(id+"F10.imprint","IMPRINT",EDGE,{"disambiguationData":[TD([[makeQuery(id+"F10.imprint","INTERSECT",VERTEX,{"derivedFrom":[subQ0,sQuery(id+"F10.wireOp",EDGE,"E19")]}),-1.0]])],"derivedFrom":subQ0})])]})]})]});}
            var Q1;
            {var subQ0=sQuery(id+"F10.wireOp",EDGE,"E17");var subQ1=sQuery(id+"F0.wireOp",EDGE,"E4");var subQ2=makeQuery(id+"F1.opExtrude","CAP_EDGE",EDGE,{"disambiguationData":[OSD([subQ1])],"isStart":false});var subQ3=sQuery(id+"F0.wireOp",EDGE,"E0");var subQ4=sQuery(id+"F2.wireOp",EDGE,"E8");var subQ5=makeQuery(id+"F2.imprint","IMPRINT",EDGE,{"disambiguationData":[TD([[makeQuery(id+"F2.imprint","INTERSECT",VERTEX,{"derivedFrom":[makeQuery(id+"F1.opExtrude","CAP_EDGE",EDGE,{"disambiguationData":[OSD([subQ3])],"isStart":false}),subQ2]}),-1.0]])],"derivedFrom":subQ2});var subQ6=makeQuery(id+"F6.opExtrude","CAP_EDGE",EDGE,{"disambiguationData":[OSD([subQ1]),TDD([subQ5])],"isStart":false});var subQ7=subQ6;var subQ8=makeQuery(id+"F7.imprint","IMPRINT",EDGE,{"disambiguationData":[TD([[makeQuery(id+"F7.imprint","INTERSECT",VERTEX,{"derivedFrom":[makeQuery(id+"F6.opExtrude","CAP_EDGE",EDGE,{"disambiguationData":[OSD([subQ4])],"isStart":false}),subQ6]}),1.0]])],"derivedFrom":subQ6});Q1=makeQuery(id+"F15.opChamfer","BLEND_EDGE",EDGE,{"blendedFrom":[makeQuery(id+"F8.boolean.opBoolean","COPY",EDGE,{"derivedFrom":makeQuery(id+"F8.opExtrude","CAP_EDGE",EDGE,{"disambiguationData":[OSD([subQ1]),TDD([subQ8])],"isStart":false})}),makeQuery(id+"F11.boolean.opBoolean","MERGE",FACE,{"derivedFrom":[makeQuery(id+"F9.boolean.opBoolean","MERGE",FACE,{"derivedFrom":[makeQuery(id+"F6.boolean.opBoolean","MERGE",FACE,{"derivedFrom":[makeQuery(id+"F3.boolean.opBoolean","SPLIT",FACE,{"disambiguationData":[TD([makeQuery(id+"F1.opExtrude","SWEPT_FACE",FACE,{"disambiguationData":[OSD([subQ3])]})])],"derivedFrom":makeQuery(id+"F1.opExtrude","SWEPT_FACE",FACE,{"disambiguationData":[OSD([subQ1])]})}),makeQuery(id+"F6.opExtrude","SWEPT_FACE",FACE,{"disambiguationData":[OSD([subQ1]),TDD([subQ5])]})]}),makeQuery(id+"F9.opExtrude","SWEPT_FACE",FACE,{"disambiguationData":[OSD([subQ1]),TDD([subQ8])]}),makeQuery(id+"F9.opExtrude","SWEPT_FACE",FACE,{"disambiguationData":[OSD([subQ1]),TDD([subQ7])]})]}),makeQuery(id+"F11.opExtrude","SWEPT_FACE",FACE,{"disambiguationData":[OSD([subQ0]),TDD([makeQuery(id+"F10.imprint","IMPRINT",EDGE,{"disambiguationData":[TD([[makeQuery(id+"F10.imprint","INTERSECT",VERTEX,{"derivedFrom":[subQ0,sQuery(id+"F10.wireOp",EDGE,"E18")]}),1.0]])],"derivedFrom":subQ0})])]})]})],"blendedInto":[makeQuery(id+"F11.boolean.opBoolean","MERGE",FACE,{"derivedFrom":[makeQuery(id+"F9.boolean.opBoolean","MERGE",FACE,{"derivedFrom":[makeQuery(id+"F6.boolean.opBoolean","MERGE",FACE,{"derivedFrom":[makeQuery(id+"F3.boolean.opBoolean","SPLIT",FACE,{"disambiguationData":[TD([makeQuery(id+"F1.opExtrude","SWEPT_FACE",FACE,{"disambiguationData":[OSD([subQ3])]})])],"derivedFrom":makeQuery(id+"F1.opExtrude","SWEPT_FACE",FACE,{"disambiguationData":[OSD([subQ1])]})}),makeQuery(id+"F6.opExtrude","SWEPT_FACE",FACE,{"disambiguationData":[OSD([subQ1]),TDD([subQ5])]})]}),makeQuery(id+"F9.opExtrude","SWEPT_FACE",FACE,{"disambiguationData":[OSD([subQ1]),TDD([subQ8])]}),makeQuery(id+"F9.opExtrude","SWEPT_FACE",FACE,{"disambiguationData":[OSD([subQ1]),TDD([subQ7])]})]}),makeQuery(id+"F11.opExtrude","SWEPT_FACE",FACE,{"disambiguationData":[OSD([subQ0]),TDD([makeQuery(id+"F10.imprint","IMPRINT",EDGE,{"disambiguationData":[TD([[makeQuery(id+"F10.imprint","INTERSECT",VERTEX,{"derivedFrom":[subQ0,sQuery(id+"F10.wireOp",EDGE,"E18")]}),1.0]])],"derivedFrom":subQ0})])]})]})]});}
            var Q2;
            {var subQ0=sQuery(id+"F10.wireOp",EDGE,"E17");var subQ1=sQuery(id+"F0.wireOp",EDGE,"E4");var subQ2=makeQuery(id+"F1.opExtrude","CAP_EDGE",EDGE,{"disambiguationData":[OSD([subQ1])],"isStart":false});var subQ3=sQuery(id+"F0.wireOp",EDGE,"E2");var subQ4=sQuery(id+"F2.wireOp",EDGE,"E9");var subQ5=makeQuery(id+"F2.imprint","IMPRINT",EDGE,{"disambiguationData":[TD([[makeQuery(id+"F2.imprint","INTERSECT",VERTEX,{"derivedFrom":[makeQuery(id+"F1.opExtrude","CAP_EDGE",EDGE,{"disambiguationData":[OSD([subQ3])],"isStart":false}),subQ2]}),1.0]])],"derivedFrom":subQ2});var subQ6=makeQuery(id+"F6.opExtrude","CAP_EDGE",EDGE,{"disambiguationData":[OSD([subQ1]),TDD([subQ5])],"isStart":false});var subQ7=subQ6;var subQ8=makeQuery(id+"F7.imprint","IMPRINT",EDGE,{"disambiguationData":[TD([[makeQuery(id+"F7.imprint","INTERSECT",VERTEX,{"derivedFrom":[makeQuery(id+"F6.opExtrude","CAP_EDGE",EDGE,{"disambiguationData":[OSD([subQ4])],"isStart":false}),subQ6]}),-1.0]])],"derivedFrom":subQ6});var subQ9=makeQuery(id+"F10.imprint","IMPRINT",EDGE,{"disambiguationData":[TD([[makeQuery(id+"F10.imprint","INTERSECT",VERTEX,{"derivedFrom":[subQ0,sQuery(id+"F10.wireOp",EDGE,"E19")]}),-1.0]])],"derivedFrom":subQ0});Q2=makeQuery(id+"F16.opChamfer","BLEND_EDGE",EDGE,{"blendedFrom":[makeQuery(id+"F11.boolean.opBoolean","MERGE",EDGE,{"derivedFrom":[makeQuery(id+"F9.boolean.opBoolean","MERGE",EDGE,{"derivedFrom":[makeQuery(id+"F9.opExtrude","CAP_EDGE",EDGE,{"disambiguationData":[OSD([subQ1]),TDD([subQ8])],"isStart":true}),makeQuery(id+"F9.opExtrude","CAP_EDGE",EDGE,{"disambiguationData":[OSD([subQ1]),TDD([subQ7])],"isStart":true})]}),makeQuery(id+"F11.opExtrude","CAP_EDGE",EDGE,{"disambiguationData":[OSD([subQ0]),TDD([subQ9])],"isStart":false})]}),makeQuery(id+"F11.boolean.opBoolean","MERGE",FACE,{"derivedFrom":[makeQuery(id+"F9.boolean.opBoolean","MERGE",FACE,{"derivedFrom":[makeQuery(id+"F6.boolean.opBoolean","MERGE",FACE,{"derivedFrom":[makeQuery(id+"F3.boolean.opBoolean","SPLIT",FACE,{"disambiguationData":[TD([makeQuery(id+"F1.opExtrude","SWEPT_FACE",FACE,{"disambiguationData":[OSD([subQ3])]})])],"derivedFrom":makeQuery(id+"F1.opExtrude","SWEPT_FACE",FACE,{"disambiguationData":[OSD([subQ1])]})}),makeQuery(id+"F6.opExtrude","SWEPT_FACE",FACE,{"disambiguationData":[OSD([subQ1]),TDD([subQ5])]})]}),makeQuery(id+"F9.opExtrude","SWEPT_FACE",FACE,{"disambiguationData":[OSD([subQ1]),TDD([subQ8])]}),makeQuery(id+"F9.opExtrude","SWEPT_FACE",FACE,{"disambiguationData":[OSD([subQ1]),TDD([subQ7])]})]}),makeQuery(id+"F11.opExtrude","SWEPT_FACE",FACE,{"disambiguationData":[OSD([subQ0]),TDD([subQ9])]})]})],"blendedInto":[makeQuery(id+"F11.boolean.opBoolean","MERGE",FACE,{"derivedFrom":[makeQuery(id+"F9.boolean.opBoolean","MERGE",FACE,{"derivedFrom":[makeQuery(id+"F6.boolean.opBoolean","MERGE",FACE,{"derivedFrom":[makeQuery(id+"F3.boolean.opBoolean","SPLIT",FACE,{"disambiguationData":[TD([makeQuery(id+"F1.opExtrude","SWEPT_FACE",FACE,{"disambiguationData":[OSD([subQ3])]})])],"derivedFrom":makeQuery(id+"F1.opExtrude","SWEPT_FACE",FACE,{"disambiguationData":[OSD([subQ1])]})}),makeQuery(id+"F6.opExtrude","SWEPT_FACE",FACE,{"disambiguationData":[OSD([subQ1]),TDD([subQ5])]})]}),makeQuery(id+"F9.opExtrude","SWEPT_FACE",FACE,{"disambiguationData":[OSD([subQ1]),TDD([subQ8])]}),makeQuery(id+"F9.opExtrude","SWEPT_FACE",FACE,{"disambiguationData":[OSD([subQ1]),TDD([subQ7])]})]}),makeQuery(id+"F11.opExtrude","SWEPT_FACE",FACE,{"disambiguationData":[OSD([subQ0]),TDD([subQ9])]})]})]});}
            var Q3;
            {var subQ0=sQuery(id+"F10.wireOp",EDGE,"E17");var subQ1=sQuery(id+"F0.wireOp",EDGE,"E4");var subQ2=makeQuery(id+"F1.opExtrude","CAP_EDGE",EDGE,{"disambiguationData":[OSD([subQ1])],"isStart":false});var subQ3=sQuery(id+"F0.wireOp",EDGE,"E0");var subQ4=sQuery(id+"F2.wireOp",EDGE,"E8");var subQ5=makeQuery(id+"F2.imprint","IMPRINT",EDGE,{"disambiguationData":[TD([[makeQuery(id+"F2.imprint","INTERSECT",VERTEX,{"derivedFrom":[makeQuery(id+"F1.opExtrude","CAP_EDGE",EDGE,{"disambiguationData":[OSD([subQ3])],"isStart":false}),subQ2]}),-1.0]])],"derivedFrom":subQ2});var subQ6=makeQuery(id+"F6.opExtrude","CAP_EDGE",EDGE,{"disambiguationData":[OSD([subQ1]),TDD([subQ5])],"isStart":false});var subQ7=subQ6;var subQ8=makeQuery(id+"F7.imprint","IMPRINT",EDGE,{"disambiguationData":[TD([[makeQuery(id+"F7.imprint","INTERSECT",VERTEX,{"derivedFrom":[makeQuery(id+"F6.opExtrude","CAP_EDGE",EDGE,{"disambiguationData":[OSD([subQ4])],"isStart":false}),subQ6]}),1.0]])],"derivedFrom":subQ6});var subQ9=makeQuery(id+"F10.imprint","IMPRINT",EDGE,{"disambiguationData":[TD([[makeQuery(id+"F10.imprint","INTERSECT",VERTEX,{"derivedFrom":[subQ0,sQuery(id+"F10.wireOp",EDGE,"E18")]}),1.0]])],"derivedFrom":subQ0});Q3=makeQuery(id+"F15.opChamfer","BLEND_EDGE",EDGE,{"blendedFrom":[makeQuery(id+"F11.boolean.opBoolean","MERGE",EDGE,{"derivedFrom":[makeQuery(id+"F9.boolean.opBoolean","MERGE",EDGE,{"derivedFrom":[makeQuery(id+"F9.opExtrude","CAP_EDGE",EDGE,{"disambiguationData":[OSD([subQ1]),TDD([subQ8])],"isStart":true}),makeQuery(id+"F9.opExtrude","CAP_EDGE",EDGE,{"disambiguationData":[OSD([subQ1]),TDD([subQ7])],"isStart":true})]}),makeQuery(id+"F11.opExtrude","CAP_EDGE",EDGE,{"disambiguationData":[OSD([subQ0]),TDD([subQ9])],"isStart":false})]}),makeQuery(id+"F11.boolean.opBoolean","MERGE",FACE,{"derivedFrom":[makeQuery(id+"F9.boolean.opBoolean","MERGE",FACE,{"derivedFrom":[makeQuery(id+"F6.boolean.opBoolean","MERGE",FACE,{"derivedFrom":[makeQuery(id+"F3.boolean.opBoolean","SPLIT",FACE,{"disambiguationData":[TD([makeQuery(id+"F1.opExtrude","SWEPT_FACE",FACE,{"disambiguationData":[OSD([subQ3])]})])],"derivedFrom":makeQuery(id+"F1.opExtrude","SWEPT_FACE",FACE,{"disambiguationData":[OSD([subQ1])]})}),makeQuery(id+"F6.opExtrude","SWEPT_FACE",FACE,{"disambiguationData":[OSD([subQ1]),TDD([subQ5])]})]}),makeQuery(id+"F9.opExtrude","SWEPT_FACE",FACE,{"disambiguationData":[OSD([subQ1]),TDD([subQ8])]}),makeQuery(id+"F9.opExtrude","SWEPT_FACE",FACE,{"disambiguationData":[OSD([subQ1]),TDD([subQ7])]})]}),makeQuery(id+"F11.opExtrude","SWEPT_FACE",FACE,{"disambiguationData":[OSD([subQ0]),TDD([subQ9])]})]})],"blendedInto":[makeQuery(id+"F11.boolean.opBoolean","MERGE",FACE,{"derivedFrom":[makeQuery(id+"F9.boolean.opBoolean","MERGE",FACE,{"derivedFrom":[makeQuery(id+"F6.boolean.opBoolean","MERGE",FACE,{"derivedFrom":[makeQuery(id+"F3.boolean.opBoolean","SPLIT",FACE,{"disambiguationData":[TD([makeQuery(id+"F1.opExtrude","SWEPT_FACE",FACE,{"disambiguationData":[OSD([subQ3])]})])],"derivedFrom":makeQuery(id+"F1.opExtrude","SWEPT_FACE",FACE,{"disambiguationData":[OSD([subQ1])]})}),makeQuery(id+"F6.opExtrude","SWEPT_FACE",FACE,{"disambiguationData":[OSD([subQ1]),TDD([subQ5])]})]}),makeQuery(id+"F9.opExtrude","SWEPT_FACE",FACE,{"disambiguationData":[OSD([subQ1]),TDD([subQ8])]}),makeQuery(id+"F9.opExtrude","SWEPT_FACE",FACE,{"disambiguationData":[OSD([subQ1]),TDD([subQ7])]})]}),makeQuery(id+"F11.opExtrude","SWEPT_FACE",FACE,{"disambiguationData":[OSD([subQ0]),TDD([subQ9])]})]})]});}
            var Q4;
            Q4=makeQuery(id+"F8.boolean.opBoolean","COPY",EDGE,{"derivedFrom":makeQuery(id+"F8.opExtrude","SWEPT_EDGE",EDGE,{"disambiguationData":[OSD([sQuery(id+"F0.wireOp",EDGE,"E4"),sQuery(id+"F7.wireOp",EDGE,"E12")])]})});
            var Q5;
            Q5=makeQuery(id+"F8.boolean.opBoolean","COPY",EDGE,{"derivedFrom":makeQuery(id+"F8.opExtrude","SWEPT_EDGE",EDGE,{"disambiguationData":[OSD([sQuery(id+"F0.wireOp",EDGE,"E4"),sQuery(id+"F7.wireOp",EDGE,"E13")])]})});
            fillet(context, id + "F17", {"entities" : qUnion([Q0, Q1, Q2, Q3, Q4, Q5]), "radius" : .5 * mm, "tangentPropagation" : true, "allowEdgeOverflow" : false});
        }
    });
